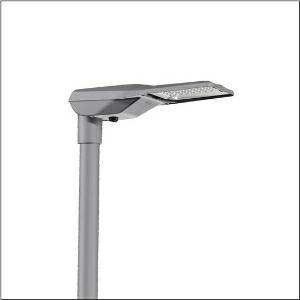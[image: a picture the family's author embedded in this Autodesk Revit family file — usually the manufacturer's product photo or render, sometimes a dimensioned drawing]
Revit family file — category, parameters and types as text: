
# Revit family: streetlight_sl_21_mini___p0_8a_5xe2u33r08gb_ec99
name_source: partatom
category: Lighting Fixtures
units: mm (PartAtom-declared; Revit-internal decimal feet)

## family parameters
Cut with Voids When Loaded = No
Host = Face
Light Source = No
Part Type = Normal
Room Calculation Point = No
Round Connector Dimension = Use Diameter
Shared = No

## types (1)
- --- (1 x LED, 5990 lm, 40.4 W, 3000K)
    Apparent Load = 40 VA
    CIE Flux Codes = 33 69 96 100 100
    Color Rendering = 70
    Color Temperature = 3000K
    Default Elevation = 1800 mm
    Description = Streetlight SL 21 mini, mast luminaire, primary light control with lens, of PMMA, primary optical cover: cover, of toughened safety glass, transparent, light distribution: P0.8a, light emission: direct distribution, primary light characteristic: asymmetric, installation type: post-top, side-entry, LED, High Power LED, rated luminous flux: 5.990lm, luminous efficacy: 148lm/W, light colour: 730, colour temperature: 3000K, control gear: D4i, control: pre-setting: logarithmic dimming characteristic, flexible luminous flux parameterisation, time-dependent luminous flux control, constant luminous flux control, overheat protection, mains connection: 220..240V, AC, 50/60Hz, start of lifetime: 40W, end of service life: 41W, reduction: 19W, luminaire housing, of diecast aluminium, powder-coated, SITECO metallic grey (DB 702S), corrosivity category C5 high according to DIN EN ISO 12944, multi-level sealing system, sealing non-destructively replaceable, inclination adjustable: 0°, 5°, 10°, 15°, please order mast flange separately, length: 628mm, width: 235mm, height: 110mm, mast flange for spigot size: 42mm (side-entry): 5XC10008XM4, 60/48mm (side-entry/post-top): 5XC10108XM2, 76/60mm (side-entry/post-top): 5XC10108XM1, mounting height: 4..8m, Smart Interface below, protection rating (complete): IP66, insulation class (complete): insulation class II (safety insulation), certification: CE, ENEC, ENEC+, VDE, impact resistance: IK10, permissible operating ambient temperature for outdoor applications: -40..+50°C, standard-compliant lighting for roads and squares, packaging unit: 1 piece

Light Distribution: P0.8a
    Height = 110 mm
    Lamp = 1 x LED
    Lamp Light Flux = 5990 lm
    Lamp Power = 40.4 W
    Lamp count = 1
    Length = 625 mm
    Luminous efficacy = 148 lm/W
    Manufacturer = Siteco
    ModVariant = No
    Model = 5XE2U33R08GB
    Number of Poles = 1
    OnlyDefault = Yes
    Power Factor = 1
    Product Name = Streetlight SL 21 mini | P0.8a
    Product group = mast luminaire | pylon top
    ProductGroupID = 6100
    Protection Class = Protection class II
    Protection Degree = IP 66
    RLX_Detail_Level = 1
    RLX_Emergency_Light_Flux = 0 lm
    RLX_Emergency_Type = 0
    RLX_Emergency_Type_DB = No
    RlxData = <blob elided: 92193 chars, md5=e174a489>
    Socket = socket
    Standby Power = 0 W
    System Light Flux = 5990 lm
    System Power = 40 W
    Type Comments = factory setting: luminous flux: 100 % | dim-lin: 254 | 812 mA
    Type Image = l_1003516.jpg
    URL = http://relux.com
    VarID = @adj_080029
    Voltage = 0 V
    Weight = 0.00 kg
    Width = 234 mm

## geometry (parser evidence)
native form markers: Blend x4, Sweep x12
no freeform markers — native parametric forms only
